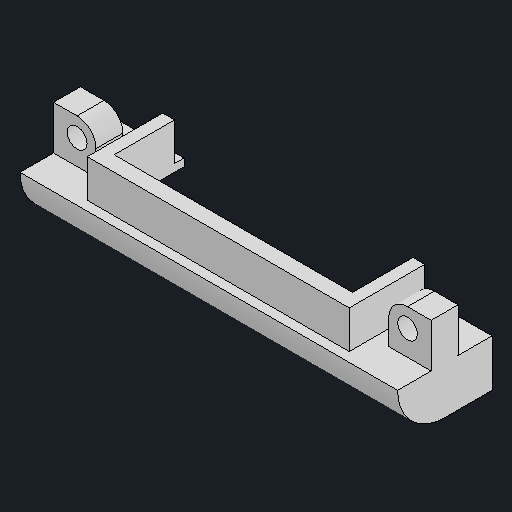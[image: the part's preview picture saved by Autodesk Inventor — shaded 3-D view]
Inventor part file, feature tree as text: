
AUTODESK INVENTOR PART (.ipt)
format: ipt  version: 2024.2 (Build 282272000, 272)  size: 117,760 bytes
history: native  units: mm
features: other x1, shell x1
ambient origin geometry x8: Origin, YZ Plane, XZ Plane, XY Plane, X Axis, Y Axis, Z Axis, Center Point
bodies: Body1 (feature_tree)
feature tree (2):
  other  "솔리드1"
  shell  "Shell1"  [1 undecoded]
note: 1 required parameter value undecoded (feature->parameter linkage not recoverable at this tier; creation-order binding heuristic only, values carry confidence <= 0.55)
